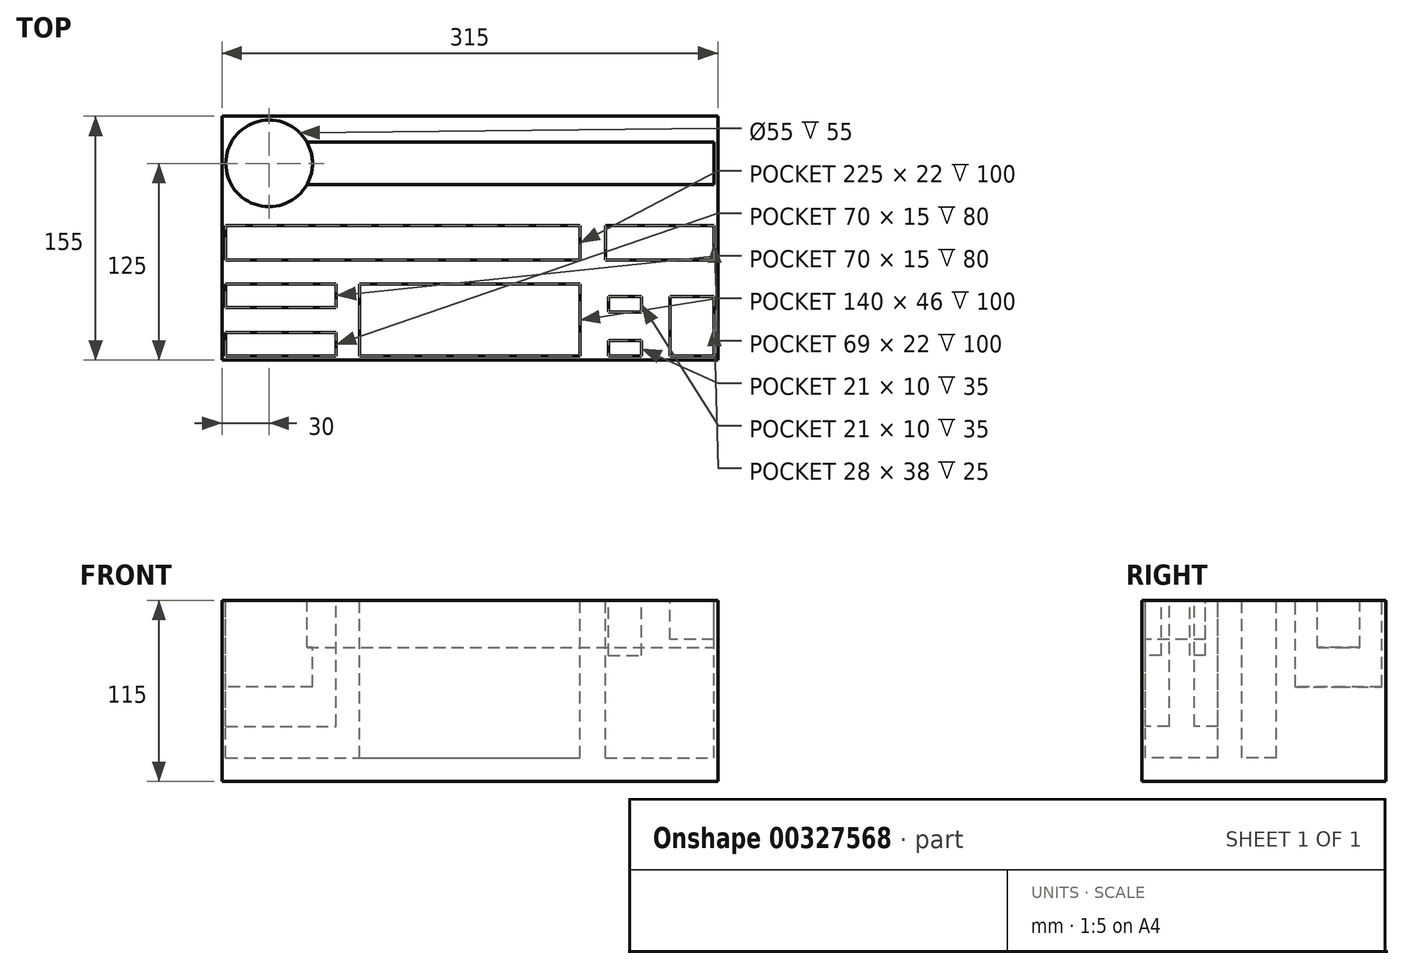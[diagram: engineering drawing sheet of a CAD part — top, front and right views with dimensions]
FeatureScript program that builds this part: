
annotation { "Feature Type Name" : "Feature", "Feature Type Description" : "" }
export const myFeature = defineFeature(function(context is Context, id is Id, definition is map)
    precondition{}
    {
        {
            var Q0;
            Q0=qCreatedBy(makeId("Top.planeOp"),FACE);
            var sketch = newSketch(context, id + "F0", { "sketchPlane" : qUnion([Q0])});
            skLineSegment(sketch, "E0.bottom", {"start": v(157.5, -77.5) * mm, "end": v(-157.5, -77.5) * mm});
            skLineSegment(sketch, "E0.top", {"start": v(157.5, 77.5) * mm, "end": v(-157.5, 77.5) * mm});
            skLineSegment(sketch, "E0.left", {"start": v(157.5, -77.5) * mm, "end": v(157.5, 77.5) * mm});
            skLineSegment(sketch, "E0.right", {"start": v(-157.5, -77.5) * mm, "end": v(-157.5, 77.5) * mm});
            skPoint(sketch, "E0.middle", {"position": v(0, 0) * mm});
            skSolve(sketch);
        }
        {
            var Q0;
            Q0 = qSketchRegion(id + "F0", true);
            extrude(context, id + "F1", {"entities" : qUnion([Q0]), "oppositeDirection" : true, "depth" : 115 * mm});
        }
        {
            var Q0;
            Q0=makeQuery(id+"F1.opExtrude","CAP_FACE",FACE,{"disambiguationData":[OSD([sQuery(id+"F0.wireOp",EDGE,"E0.bottom"),sQuery(id+"F0.wireOp",EDGE,"E0.top"),sQuery(id+"F0.wireOp",EDGE,"E0.left"),sQuery(id+"F0.wireOp",EDGE,"E0.right")])],"isStart":true});
            var sketch = newSketch(context, id + "F2", { "sketchPlane" : qUnion([Q0])});
            skCircle(sketch, "E1", {"center": v(-127.5, 47.5) * mm, "radius": 27.5 * mm});
            skLineSegment(sketch, "E2.bottom", {"start": v(-103.54, 61) * mm, "end": v(155, 61) * mm});
            skLineSegment(sketch, "E2.top", {"start": v(-103.54, 34) * mm, "end": v(155, 34) * mm});
            skLineSegment(sketch, "E2.right", {"start": v(155, 61) * mm, "end": v(155, 34) * mm});
            skSolve(sketch);
        }
        {
            var Q0;
            {var subQ1=sQuery(id+"F2.wireOp",EDGE,"E2.bottom");Q0=makeQuery(id+"F2.imprint","IMPRINT",FACE,{"disambiguationData":[TD([[makeQuery(id+"F2.imprint","IMPRINT",EDGE,{"derivedFrom":subQ1}),1.0]])]});}
            var sketch = newSketch(context, id + "F3", { "sketchPlane" : qUnion([Q0])});
            skLineSegment(sketch, "E3.bottom", {"start": v(-155, 8) * mm, "end": v(70, 8) * mm});
            skLineSegment(sketch, "E3.top", {"start": v(-155, -14) * mm, "end": v(70, -14) * mm});
            skLineSegment(sketch, "E3.left", {"start": v(-155, 8) * mm, "end": v(-155, -14) * mm});
            skLineSegment(sketch, "E3.right", {"start": v(70, 8) * mm, "end": v(70, -14) * mm});
            skSolve(sketch);
        }
        {
            var Q0;
            {var subQ1=sQuery(id+"F2.wireOp",EDGE,"E2.bottom");Q0=makeQuery(id+"F2.imprint","IMPRINT",FACE,{"disambiguationData":[TD([[makeQuery(id+"F2.imprint","IMPRINT",EDGE,{"derivedFrom":subQ1}),1.0]])]});}
            var sketch = newSketch(context, id + "F4", { "sketchPlane" : qUnion([Q0])});
            skLineSegment(sketch, "E4.bottom", {"start": v(-155, -29) * mm, "end": v(-85, -29) * mm});
            skLineSegment(sketch, "E4.top", {"start": v(-155, -44) * mm, "end": v(-85, -44) * mm});
            skLineSegment(sketch, "E4.left", {"start": v(-155, -29) * mm, "end": v(-155, -44) * mm});
            skLineSegment(sketch, "E4.right", {"start": v(-85, -29) * mm, "end": v(-85, -44) * mm});
            skLineSegment(sketch, "E5.bottom", {"start": v(-155, -60) * mm, "end": v(-85, -60) * mm});
            skLineSegment(sketch, "E5.top", {"start": v(-155, -75) * mm, "end": v(-85, -75) * mm});
            skLineSegment(sketch, "E5.left", {"start": v(-155, -60) * mm, "end": v(-155, -75) * mm});
            skLineSegment(sketch, "E5.right", {"start": v(-85, -60) * mm, "end": v(-85, -75) * mm});
            skSolve(sketch);
        }
        {
            var Q0;
            {var subQ1=sQuery(id+"F2.wireOp",EDGE,"E2.bottom");Q0=makeQuery(id+"F2.imprint","IMPRINT",FACE,{"disambiguationData":[TD([[makeQuery(id+"F2.imprint","IMPRINT",EDGE,{"derivedFrom":subQ1}),1.0]])]});}
            var sketch = newSketch(context, id + "F5", { "sketchPlane" : qUnion([Q0])});
            skLineSegment(sketch, "E6.bottom", {"start": v(-70, -29) * mm, "end": v(70, -29) * mm});
            skLineSegment(sketch, "E6.top", {"start": v(-70, -75) * mm, "end": v(70, -75) * mm});
            skLineSegment(sketch, "E6.left", {"start": v(-70, -29) * mm, "end": v(-70, -75) * mm});
            skLineSegment(sketch, "E6.right", {"start": v(70, -29) * mm, "end": v(70, -75) * mm});
            skSolve(sketch);
        }
        {
            var Q0;
            {var subQ1=sQuery(id+"F2.wireOp",EDGE,"E2.bottom");Q0=makeQuery(id+"F2.imprint","IMPRINT",FACE,{"disambiguationData":[TD([[makeQuery(id+"F2.imprint","IMPRINT",EDGE,{"derivedFrom":subQ1}),1.0]])]});}
            var sketch = newSketch(context, id + "F6", { "sketchPlane" : qUnion([Q0])});
            skLineSegment(sketch, "E7.bottom", {"start": v(86, 8) * mm, "end": v(155, 8) * mm});
            skLineSegment(sketch, "E7.top", {"start": v(86, -14) * mm, "end": v(155, -14) * mm});
            skLineSegment(sketch, "E7.left", {"start": v(86, 8) * mm, "end": v(86, -14) * mm});
            skLineSegment(sketch, "E7.right", {"start": v(155, 8) * mm, "end": v(155, -14) * mm});
            skSolve(sketch);
        }
        {
            var Q0;
            {var subQ1=sQuery(id+"F2.wireOp",EDGE,"E2.bottom");Q0=makeQuery(id+"F2.imprint","IMPRINT",FACE,{"disambiguationData":[TD([[makeQuery(id+"F2.imprint","IMPRINT",EDGE,{"derivedFrom":subQ1}),1.0]])]});}
            var sketch = newSketch(context, id + "F7", { "sketchPlane" : qUnion([Q0])});
            skLineSegment(sketch, "E8.bottom", {"start": v(88, -37) * mm, "end": v(109, -37) * mm});
            skLineSegment(sketch, "E8.top", {"start": v(88, -47) * mm, "end": v(109, -47) * mm});
            skLineSegment(sketch, "E8.left", {"start": v(88, -37) * mm, "end": v(88, -47) * mm});
            skLineSegment(sketch, "E8.right", {"start": v(109, -37) * mm, "end": v(109, -47) * mm});
            skLineSegment(sketch, "E9.bottom", {"start": v(88, -65) * mm, "end": v(109, -65) * mm});
            skLineSegment(sketch, "E9.top", {"start": v(88, -75) * mm, "end": v(109, -75) * mm});
            skLineSegment(sketch, "E9.left", {"start": v(88, -65) * mm, "end": v(88, -75) * mm});
            skLineSegment(sketch, "E9.right", {"start": v(109, -65) * mm, "end": v(109, -75) * mm});
            skSolve(sketch);
        }
        {
            var Q0;
            {var subQ1=sQuery(id+"F2.wireOp",EDGE,"E2.bottom");Q0=makeQuery(id+"F2.imprint","IMPRINT",FACE,{"disambiguationData":[TD([[makeQuery(id+"F2.imprint","IMPRINT",EDGE,{"derivedFrom":subQ1}),1.0]])]});}
            var sketch = newSketch(context, id + "F8", { "sketchPlane" : qUnion([Q0])});
            skLineSegment(sketch, "E10.bottom", {"start": v(155, -37) * mm, "end": v(127, -37) * mm});
            skLineSegment(sketch, "E10.top", {"start": v(155, -75) * mm, "end": v(127, -75) * mm});
            skLineSegment(sketch, "E10.left", {"start": v(155, -37) * mm, "end": v(155, -75) * mm});
            skLineSegment(sketch, "E10.right", {"start": v(127, -37) * mm, "end": v(127, -75) * mm});
            skSolve(sketch);
        }
        {
            var Q0;
            Q0 = qSketchRegion(id + "F3", true);
            extrude(context, id + "F9", {"entities" : qUnion([Q0]), "operationType" : NewBodyOperationType.REMOVE, "oppositeDirection" : true, "depth" : 100 * mm});
        }
        {
            var Q0;
            {var subQ0=sQuery(id+"F2.wireOp",EDGE,"E1");var subQ1=makeQuery(id+"F2.imprint","INTERSECT",VERTEX,{"derivedFrom":[subQ0,sQuery(id+"F2.wireOp",EDGE,"E2.bottom")]});Q0=makeQuery(id+"F2.imprint","IMPRINT",FACE,{"disambiguationData":[TD([[makeQuery(id+"F2.imprint","IMPRINT",EDGE,{"disambiguationData":[TD([[subQ1,-1.0]])],"derivedFrom":subQ0}),1.0]])]});}
            extrude(context, id + "F10", {"entities" : qUnion([Q0]), "operationType" : NewBodyOperationType.REMOVE, "oppositeDirection" : true, "depth" : 55 * mm});
        }
        {
            var Q0;
            {var subQ0=sQuery(id+"F2.wireOp",EDGE,"E2.bottom");Q0=makeQuery(id+"F4.imprint","IMPRINT",FACE,{"disambiguationData":[TD([[makeQuery(id+"F4.imprint","IMPRINT",EDGE,{"derivedFrom":makeQuery(id+"F2.imprint","IMPRINT",EDGE,{"derivedFrom":subQ0})}),-1.0]])]});}
            extrude(context, id + "F11", {"entities" : qUnion([Q0]), "operationType" : NewBodyOperationType.REMOVE, "oppositeDirection" : true, "depth" : 30 * mm});
        }
        {
            var Q0;
            Q0 = qSketchRegion(id + "F4", true);
            extrude(context, id + "F12", {"entities" : qUnion([Q0]), "operationType" : NewBodyOperationType.REMOVE, "oppositeDirection" : true, "depth" : 80 * mm});
        }
        {
            var Q0;
            Q0 = qSketchRegion(id + "F5", true);
            extrude(context, id + "F13", {"entities" : qUnion([Q0]), "operationType" : NewBodyOperationType.REMOVE, "oppositeDirection" : true, "depth" : 100 * mm});
        }
        {
            var Q0;
            Q0 = qSketchRegion(id + "F6", true);
            extrude(context, id + "F14", {"entities" : qUnion([Q0]), "operationType" : NewBodyOperationType.REMOVE, "oppositeDirection" : true, "depth" : 100 * mm});
        }
        {
            var Q0;
            Q0 = qSketchRegion(id + "F7", true);
            extrude(context, id + "F15", {"entities" : qUnion([Q0]), "operationType" : NewBodyOperationType.REMOVE, "oppositeDirection" : true, "depth" : 35 * mm});
        }
        {
            var Q0;
            Q0 = qSketchRegion(id + "F8", true);
            extrude(context, id + "F16", {"entities" : qUnion([Q0]), "operationType" : NewBodyOperationType.REMOVE, "oppositeDirection" : true, "depth" : 25 * mm});
        }
    });
